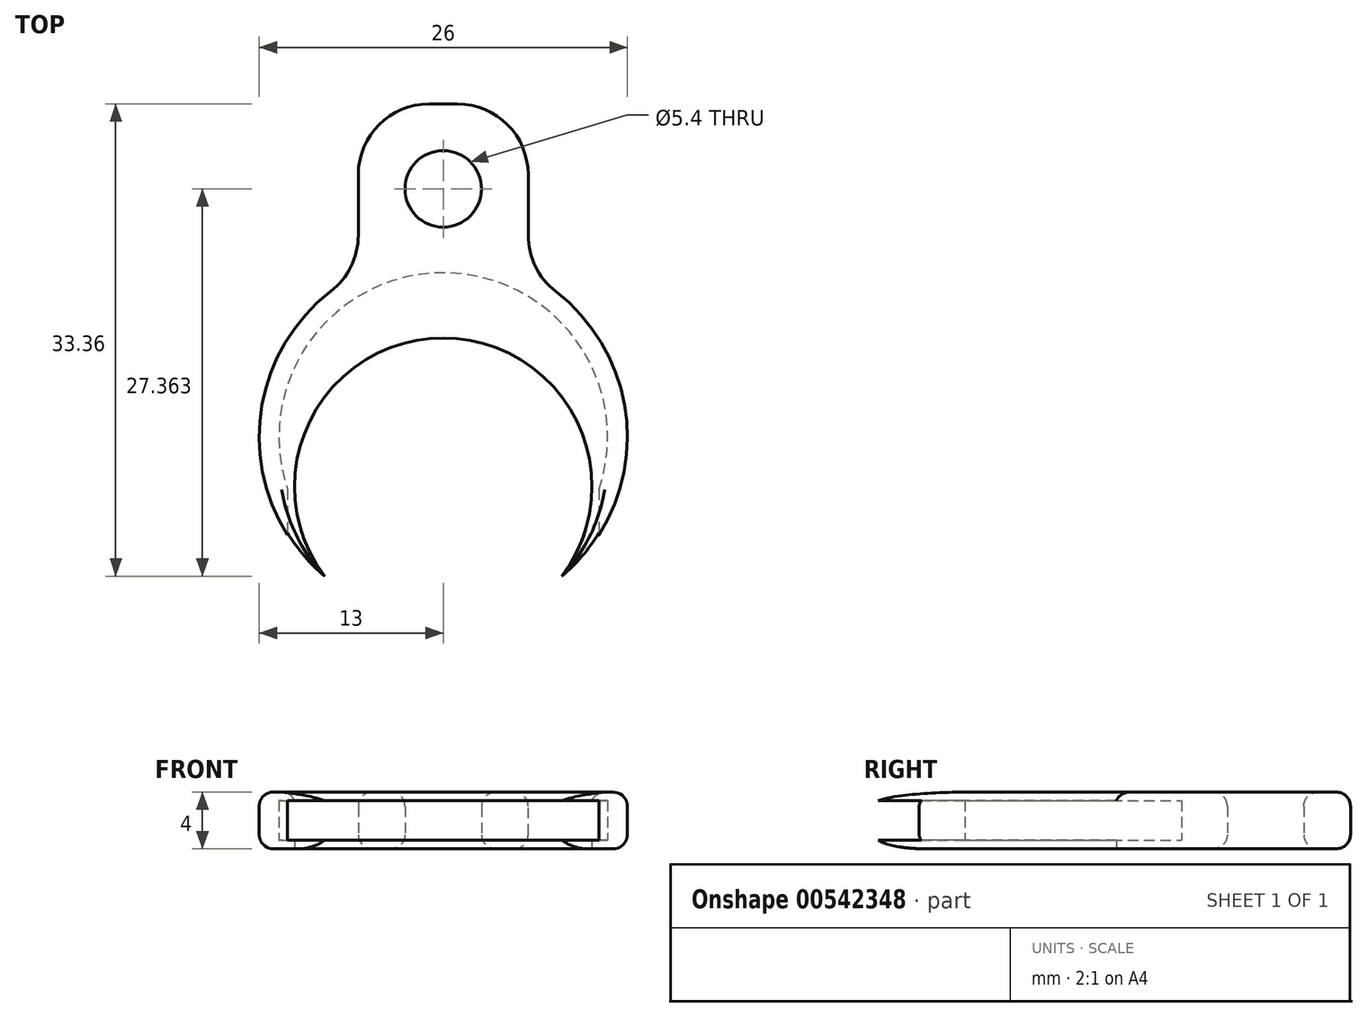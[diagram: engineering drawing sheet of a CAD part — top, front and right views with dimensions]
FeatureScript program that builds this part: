
annotation { "Feature Type Name" : "Feature", "Feature Type Description" : "" }
export const myFeature = defineFeature(function(context is Context, id is Id, definition is map)
    precondition{}
    {
        {
            var Q0;
            Q0=qCreatedBy(makeId("Top.planeOp"),FACE);
            var sketch = newSketch(context, id + "F0", { "sketchPlane" : qUnion([Q0])});
            skCircle(sketch, "E0", {"center": v(0, 0) * mm, "radius": 13 * mm});
            skLineSegment(sketch, "E1.bottom", {"start": v(-6, 11.53) * mm, "end": v(6, 11.53) * mm});
            skLineSegment(sketch, "E1.top", {"start": v(-6, 23.53) * mm, "end": v(6, 23.53) * mm});
            skLineSegment(sketch, "E1.left", {"start": v(-6, 11.53) * mm, "end": v(-6, 23.53) * mm});
            skLineSegment(sketch, "E1.right", {"start": v(6, 11.53) * mm, "end": v(6, 23.53) * mm});
            skCircle(sketch, "E2", {"center": v(0, 17.53) * mm, "radius": 2.7 * mm});
            skSolve(sketch);
        }
        {
            var Q0;
            Q0 = qSketchRegion(id + "F0", true);
            extrude(context, id + "F1", {"entities" : qUnion([Q0]), "endBound" : BoundingType.SYMMETRIC, "depth" : 4 * mm, "offsetDistance" : 25 * mm});
        }
        {
            var Q0;
            Q0=makeQuery(id+"F1.opExtrude","SWEPT_EDGE",EDGE,{"disambiguationData":[OSD([sQuery(id+"F0.wireOp",EDGE,"E0"),sQuery(id+"F0.wireOp",EDGE,"E1.bottom"),sQuery(id+"F0.wireOp",EDGE,"E1.right")])]});
            var Q1;
            Q1=makeQuery(id+"F1.opExtrude","SWEPT_EDGE",EDGE,{"disambiguationData":[OSD([sQuery(id+"F0.wireOp",EDGE,"E1.top"),sQuery(id+"F0.wireOp",EDGE,"E1.right")])]});
            var Q2;
            Q2=makeQuery(id+"F1.opExtrude","SWEPT_EDGE",EDGE,{"disambiguationData":[OSD([sQuery(id+"F0.wireOp",EDGE,"E1.top"),sQuery(id+"F0.wireOp",EDGE,"E1.left")])]});
            var Q3;
            Q3=makeQuery(id+"F1.opExtrude","SWEPT_EDGE",EDGE,{"disambiguationData":[OSD([sQuery(id+"F0.wireOp",EDGE,"E0"),sQuery(id+"F0.wireOp",EDGE,"E1.bottom"),sQuery(id+"F0.wireOp",EDGE,"E1.left")])]});
            fillet(context, id + "F2", {"entities" : qUnion([Q0, Q1, Q2, Q3]), "radius" : 5 * mm, "tangentPropagation" : true, "allowEdgeOverflow" : false});
        }
        {
            var Q0;
            Q0=makeQuery(id+"F1.opExtrude","CAP_EDGE",EDGE,{"disambiguationData":[OSD([sQuery(id+"F0.wireOp",EDGE,"E2")])],"isStart":true});
            var Q1;
            Q1=makeQuery(id+"F1.opExtrude","CAP_EDGE",EDGE,{"disambiguationData":[OSD([sQuery(id+"F0.wireOp",EDGE,"E2")])],"isStart":false});
            fillet(context, id + "F3", {"entities" : qUnion([Q0, Q1]), "radius" : 1 * mm, "tangentPropagation" : true, "allowEdgeOverflow" : false});
        }
        {
            var Q0;
            Q0=makeQuery(id+"F1.opExtrude","CAP_FACE",FACE,{"disambiguationData":[OSD([sQuery(id+"F0.wireOp",EDGE,"E0"),sQuery(id+"F0.wireOp",EDGE,"E1.top"),sQuery(id+"F0.wireOp",EDGE,"E1.left"),sQuery(id+"F0.wireOp",EDGE,"E1.right"),sQuery(id+"F0.wireOp",EDGE,"E2")])],"isStart":true});
            var sketch = newSketch(context, id + "F4", { "sketchPlane" : qUnion([Q0])});
            skCircle(sketch, "E3", {"center": v(0, 3.5) * mm, "radius": 10.5 * mm});
            skSolve(sketch);
        }
        {
            var Q0;
            Q0 = qSketchRegion(id + "F4", true);
            extrude(context, id + "F5", {"entities" : qUnion([Q0]), "operationType" : NewBodyOperationType.REMOVE, "endBound" : BoundingType.THROUGH_ALL, "oppositeDirection" : true, "depth" : 25 * mm, "offsetDistance" : 25 * mm});
        }
        {
            var Q0;
            Q0=qCreatedBy(makeId("Top.planeOp"),FACE);
            var sketch = newSketch(context, id + "F6", { "sketchPlane" : qUnion([Q0])});
            skCircle(sketch, "E4", {"center": v(0, 0) * mm, "radius": 11.6 * mm});
            skLineSegment(sketch, "E5.bottom", {"start": v(-11, -3.7) * mm, "end": v(11, -3.7) * mm});
            skLineSegment(sketch, "E5.top", {"start": v(-11, -14.56) * mm, "end": v(11, -14.56) * mm});
            skLineSegment(sketch, "E5.left", {"start": v(-11, -3.7) * mm, "end": v(-11, -14.56) * mm});
            skLineSegment(sketch, "E5.right", {"start": v(11, -3.7) * mm, "end": v(11, -14.56) * mm});
            skSolve(sketch);
        }
        {
            var Q0;
            Q0 = qSketchRegion(id + "F6", true);
            extrude(context, id + "F7", {"entities" : qUnion([Q0]), "operationType" : NewBodyOperationType.REMOVE, "endBound" : BoundingType.SYMMETRIC, "depth" : 2.8 * mm, "offsetDistance" : 25 * mm});
        }
        {
            var Q0;
            {var subQ0=sQuery(id+"F0.wireOp",EDGE,"E0");var subQ1=sQuery(id+"F0.wireOp",EDGE,"E1.right");Q0=makeQuery(id+"F5.boolean.opBoolean","SPLIT",EDGE,{"disambiguationData":[TD([makeQuery(id+"F2.opFillet","BLEND_FACE",FACE,{"disambiguationData":[OSD([subQ0,sQuery(id+"F0.wireOp",EDGE,"E1.bottom"),subQ1])]})])],"derivedFrom":makeQuery(id+"F1.opExtrude","CAP_EDGE",EDGE,{"disambiguationData":[OSD([subQ0])],"isStart":false})});}
            var Q1;
            {var subQ0=sQuery(id+"F0.wireOp",EDGE,"E1.right");var subQ1=sQuery(id+"F0.wireOp",EDGE,"E0");Q1=makeQuery(id+"F2.opFillet","BLEND_EDGE",EDGE,{"blendedFrom":[makeQuery(id+"F1.opExtrude","SWEPT_EDGE",EDGE,{"disambiguationData":[OSD([subQ1,sQuery(id+"F0.wireOp",EDGE,"E1.bottom"),subQ0])]}),makeQuery(id+"F1.opExtrude","CAP_FACE",FACE,{"disambiguationData":[OSD([subQ1,sQuery(id+"F0.wireOp",EDGE,"E1.top"),sQuery(id+"F0.wireOp",EDGE,"E1.left"),subQ0,sQuery(id+"F0.wireOp",EDGE,"E2")])],"isStart":false})],"blendedInto":[makeQuery(id+"F1.opExtrude","CAP_FACE",FACE,{"disambiguationData":[OSD([subQ1,sQuery(id+"F0.wireOp",EDGE,"E1.top"),sQuery(id+"F0.wireOp",EDGE,"E1.left"),subQ0,sQuery(id+"F0.wireOp",EDGE,"E2")])],"isStart":false})]});}
            var Q2;
            Q2=makeQuery(id+"F1.opExtrude","CAP_EDGE",EDGE,{"disambiguationData":[OSD([sQuery(id+"F0.wireOp",EDGE,"E1.right")])],"isStart":false});
            var Q3;
            {var subQ0=sQuery(id+"F0.wireOp",EDGE,"E1.right");var subQ1=sQuery(id+"F0.wireOp",EDGE,"E1.top");Q3=makeQuery(id+"F2.opFillet","BLEND_EDGE",EDGE,{"blendedFrom":[makeQuery(id+"F1.opExtrude","SWEPT_EDGE",EDGE,{"disambiguationData":[OSD([subQ1,subQ0])]}),makeQuery(id+"F1.opExtrude","CAP_FACE",FACE,{"disambiguationData":[OSD([sQuery(id+"F0.wireOp",EDGE,"E0"),subQ1,sQuery(id+"F0.wireOp",EDGE,"E1.left"),subQ0,sQuery(id+"F0.wireOp",EDGE,"E2")])],"isStart":false})],"blendedInto":[makeQuery(id+"F1.opExtrude","CAP_FACE",FACE,{"disambiguationData":[OSD([sQuery(id+"F0.wireOp",EDGE,"E0"),subQ1,sQuery(id+"F0.wireOp",EDGE,"E1.left"),subQ0,sQuery(id+"F0.wireOp",EDGE,"E2")])],"isStart":false})]});}
            var Q4;
            {var subQ0=sQuery(id+"F0.wireOp",EDGE,"E0");var subQ1=sQuery(id+"F0.wireOp",EDGE,"E1.left");Q4=makeQuery(id+"F5.boolean.opBoolean","SPLIT",EDGE,{"disambiguationData":[TD([makeQuery(id+"F2.opFillet","BLEND_FACE",FACE,{"disambiguationData":[OSD([subQ0,sQuery(id+"F0.wireOp",EDGE,"E1.bottom"),subQ1])]})])],"derivedFrom":makeQuery(id+"F1.opExtrude","CAP_EDGE",EDGE,{"disambiguationData":[OSD([subQ0])],"isStart":true})});}
            var Q5;
            Q5=makeQuery(id+"F5.boolean.opBoolean","COPY",EDGE,{"derivedFrom":makeQuery(id+"F5.opExtrude","CAP_EDGE",EDGE,{"disambiguationData":[OSD([sQuery(id+"F4.wireOp",EDGE,"E3")])],"isStart":true})});
            var Q6;
            Q6=makeQuery(id+"F5.boolean.opBoolean","INTERSECT",EDGE,{"derivedFrom":[makeQuery(id+"F1.opExtrude","CAP_FACE",FACE,{"disambiguationData":[OSD([sQuery(id+"F0.wireOp",EDGE,"E0"),sQuery(id+"F0.wireOp",EDGE,"E1.top"),sQuery(id+"F0.wireOp",EDGE,"E1.left"),sQuery(id+"F0.wireOp",EDGE,"E1.right"),sQuery(id+"F0.wireOp",EDGE,"E2")])],"isStart":false}),makeQuery(id+"F5.opExtrude","SWEPT_FACE",FACE,{"disambiguationData":[OSD([sQuery(id+"F4.wireOp",EDGE,"E3")])]})]});
            fillet(context, id + "F8", {"entities" : qUnion([Q0, Q1, Q2, Q3, Q4, Q5, Q6]), "radius" : 1 * mm, "tangentPropagation" : true, "allowEdgeOverflow" : false});
        }
    });
